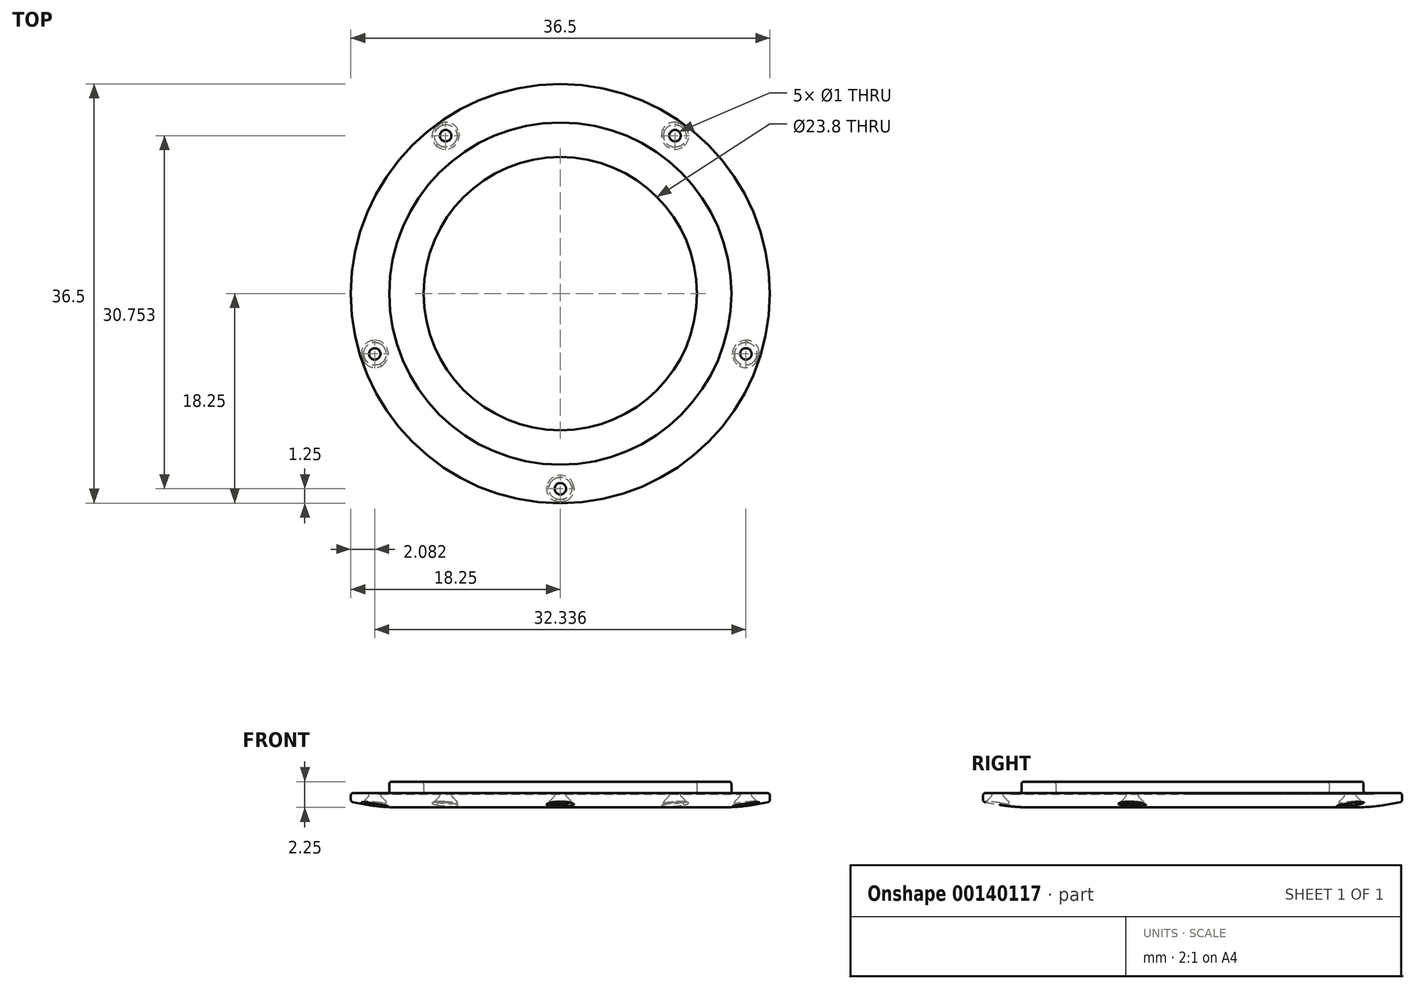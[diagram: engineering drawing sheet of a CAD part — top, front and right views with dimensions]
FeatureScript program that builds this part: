
annotation { "Feature Type Name" : "Feature", "Feature Type Description" : "" }
export const myFeature = defineFeature(function(context is Context, id is Id, definition is map)
    precondition{}
    {
        {
            var Q0;
            Q0=qCreatedBy(makeId("Front.planeOp"),FACE);
            var sketch = newSketch(context, id + "F0", { "sketchPlane" : qUnion([Q0])});
            skLineSegment(sketch, "E0", {"start": v(0, 0) * mm, "end": v(0, -1.25) * mm});
            skLineSegment(sketch, "E1", {"start": v(0, 0) * mm, "end": v(-11.7, 0) * mm});
            skLineSegment(sketch, "E2", {"start": v(-11.9, 0.2) * mm, "end": v(-11.9, 0.8) * mm});
            skLineSegment(sketch, "E3", {"start": v(-12.1, 1) * mm, "end": v(-14.7, 1) * mm});
            skLineSegment(sketch, "E4", {"start": v(-14.9, 0.8) * mm, "end": v(-14.9, 0.2) * mm});
            skLineSegment(sketch, "E5", {"start": v(-15.1, 0) * mm, "end": v(-15.47, 0) * mm});
            skLineSegment(sketch, "E6", {"start": v(-18.25, -0.2) * mm, "end": v(-18.25, -0.6) * mm});
            skLineSegment(sketch, "E7", {"start": v(-14, -1.25) * mm, "end": v(0, -1.25) * mm});
            skLineSegment(sketch, "E8", {"start": v(0, 0) * mm, "end": v(0, 1) * mm, "construction": true});
            skArc(sketch, "E9", {"start": v(-14, -1.25) * mm, "mid": v(-16.06, -1.13) * mm, "end": v(-18.1, -0.79) * mm});
            skPoint(sketch, "E10.visualSharp", {"position": v(-14.9, 0) * mm});
            skArc(sketch, "E10.filletArc", {"start": v(-15.1, 0) * mm, "mid": v(-14.96, 0.06) * mm, "end": v(-14.9, 0.2) * mm});
            skPoint(sketch, "E11.visualSharp", {"position": v(-14.9, 1) * mm});
            skArc(sketch, "E11.filletArc", {"start": v(-14.7, 1) * mm, "mid": v(-14.84, 0.94) * mm, "end": v(-14.9, 0.8) * mm});
            skPoint(sketch, "E12.visualSharp", {"position": v(-11.9, 0) * mm});
            skArc(sketch, "E12.filletArc", {"start": v(-11.9, 0.2) * mm, "mid": v(-11.84, 0.06) * mm, "end": v(-11.7, 0) * mm});
            skPoint(sketch, "E13.visualSharp", {"position": v(-18.25, 0) * mm});
            skArc(sketch, "E13.filletArc", {"start": v(-18.05, 0) * mm, "mid": v(-18.2, -0.06) * mm, "end": v(-18.25, -0.2) * mm});
            skPoint(sketch, "E14.visualSharp", {"position": v(-18.25, -0.75) * mm});
            skArc(sketch, "E14.filletArc", {"start": v(-18.25, -0.6) * mm, "mid": v(-18.2, -0.72) * mm, "end": v(-18.1, -0.79) * mm});
            skPoint(sketch, "E15.visualSharp", {"position": v(-11.9, 1) * mm});
            skArc(sketch, "E15.filletArc", {"start": v(-11.9, 0.8) * mm, "mid": v(-11.96, 0.94) * mm, "end": v(-12.1, 1) * mm});
            skPoint(sketch, "E16.visualSharp", {"position": v(0, -1.25) * mm});
            skArc(sketch, "E17", {"start": v(-15.9, -0.04) * mm, "mid": v(-15.75, -0.1) * mm, "end": v(-15.6, -0.04) * mm});
            skLineSegment(sketch, "E18.trimOffspring", {"start": v(-16.03, 0) * mm, "end": v(-18.05, 0) * mm});
            skPoint(sketch, "E19.visualSharp", {"position": v(-15.95, 0) * mm});
            skArc(sketch, "E19.filletArc", {"start": v(-15.9, -0.04) * mm, "mid": v(-15.97, -0.01) * mm, "end": v(-16.03, 0) * mm});
            skPoint(sketch, "E20.visualSharp", {"position": v(-15.55, 0) * mm});
            skArc(sketch, "E20.filletArc", {"start": v(-15.47, 0) * mm, "mid": v(-15.53, -0.01) * mm, "end": v(-15.6, -0.04) * mm});
            skSolve(sketch);
        }
        {
            var Q0;
            Q0=qSketchRegion(id+"F0",true);
            var Q1;
            Q1=sQuery(id+"F0.wireOp",EDGE,"E8");
            revolve(context, id + "F1", {"entities" : qUnion([Q0]), "axis" : qUnion([Q1]), "revolveType" : RevolveType.FULL});
        }
        {
            var Q0;
            Q0=qCreatedBy(makeId("Right.planeOp"),FACE);
            var sketch = newSketch(context, id + "F2", { "sketchPlane" : qUnion([Q0])});
            skLineSegment(sketch, "E21", {"start": v(-17, 0) * mm, "end": v(-17.5, 0) * mm});
            skLineSegment(sketch, "E22", {"start": v(-17, -1.25) * mm, "end": v(-18, -1.25) * mm});
            skLineSegment(sketch, "E23", {"start": v(-18, -1.25) * mm, "end": v(-18, -0.75) * mm});
            skLineSegment(sketch, "E24", {"start": v(-17, 0) * mm, "end": v(-17, 0.93) * mm, "construction": true});
            skLineSegment(sketch, "E25", {"start": v(-17, 0) * mm, "end": v(-17, -1.25) * mm});
            skLineSegment(sketch, "E26", {"start": v(-17.5, 0) * mm, "end": v(-17.5, -0.25) * mm});
            skLineSegment(sketch, "E27", {"start": v(-17.5, -0.25) * mm, "end": v(-18, -0.75) * mm});
            skSolve(sketch);
        }
        {
            var Q0;
            Q0=qSketchRegion(id+"F2",true);
            var Q1;
            Q1=makeQuery(id+"F2.imprint","IMPRINT",FACE,{"disambiguationData":[TD([[makeQuery(id+"F2.imprint","IMPRINT",EDGE,{"derivedFrom":sQuery(id+"F2.wireOp",EDGE,"E21")}),1.0]])]});
            var Q2;
            Q2=sQuery(id+"F2.wireOp",EDGE,"E24");
            revolve(context, id + "F3", {"entities" : qUnion([Q0, Q1]), "axis" : qUnion([Q2]), "revolveType" : RevolveType.FULL, "oppositeDirection" : true});
        }
        {
            var Q0;
            Q0=makeQuery(id+"F3.opRevolve","SWEPT_BODY",BODY,{"disambiguationData":[OSD([sQuery(id+"F2.wireOp",EDGE,"E21"),sQuery(id+"F2.wireOp",EDGE,"2oNXKCKB-Rh66-Nj45-adpD-4nFgSYGKnnpU"),sQuery(id+"F2.wireOp",EDGE,"E22"),sQuery(id+"F2.wireOp",EDGE,"E23"),sQuery(id+"F2.wireOp",EDGE,"tctMOU8y-Mgo1-Lk33-zD8C-WWPehcmeRYiv"),sQuery(id+"F2.wireOp",EDGE,"E25")])]});
            var Q1;
            Q1=makeQuery(id+"F1.opRevolve","SWEPT_EDGE",EDGE,{"disambiguationData":[OSD([sQuery(id+"F0.wireOp",EDGE,"E7"),sQuery(id+"F0.wireOp",EDGE,"E9")])]});
            circularPattern(context, id + "F4", {"operationType" : NewBodyOperationType.REMOVE, "entities" : qUnion([Q0]), "axis" : qUnion([Q1]), "angle" : 360 * degree, "instanceCount" : 5, "equalSpace" : true, "computeTransformsWithoutBuiltin" : true});
        }
        {
            var Q0;
            Q0=makeQuery(id+"F4.boolean.opBoolean","COPY",EDGE,{"derivedFrom":makeQuery(id+"F4.opPattern","COPY",EDGE,{"derivedFrom":makeQuery(id+"F3.opRevolve","SWEPT_EDGE",EDGE,{"disambiguationData":[OSD([sQuery(id+"F2.wireOp",EDGE,"E21"),sQuery(id+"F2.wireOp",EDGE,"tctMOU8y-Mgo1-Lk33-zD8C-WWPehcmeRYiv")])]}),"instanceName":"1"})});
            var Q1;
            Q1=makeQuery(id+"F4.boolean.opBoolean","COPY",EDGE,{"derivedFrom":makeQuery(id+"F3.opRevolve","SWEPT_EDGE",EDGE,{"disambiguationData":[OSD([sQuery(id+"F2.wireOp",EDGE,"E21"),sQuery(id+"F2.wireOp",EDGE,"tctMOU8y-Mgo1-Lk33-zD8C-WWPehcmeRYiv")])]})});
            var Q2;
            Q2=makeQuery(id+"F4.boolean.opBoolean","COPY",EDGE,{"derivedFrom":makeQuery(id+"F4.opPattern","COPY",EDGE,{"derivedFrom":makeQuery(id+"F3.opRevolve","SWEPT_EDGE",EDGE,{"disambiguationData":[OSD([sQuery(id+"F2.wireOp",EDGE,"E21"),sQuery(id+"F2.wireOp",EDGE,"tctMOU8y-Mgo1-Lk33-zD8C-WWPehcmeRYiv")])]}),"instanceName":"3"})});
            var Q3;
            Q3=makeQuery(id+"F4.boolean.opBoolean","COPY",EDGE,{"derivedFrom":makeQuery(id+"F4.opPattern","COPY",EDGE,{"derivedFrom":makeQuery(id+"F3.opRevolve","SWEPT_EDGE",EDGE,{"disambiguationData":[OSD([sQuery(id+"F2.wireOp",EDGE,"E21"),sQuery(id+"F2.wireOp",EDGE,"tctMOU8y-Mgo1-Lk33-zD8C-WWPehcmeRYiv")])]}),"instanceName":"2"})});
            var Q4;
            Q4=makeQuery(id+"F4.boolean.opBoolean","COPY",EDGE,{"derivedFrom":makeQuery(id+"F4.opPattern","COPY",EDGE,{"derivedFrom":makeQuery(id+"F3.opRevolve","SWEPT_EDGE",EDGE,{"disambiguationData":[OSD([sQuery(id+"F2.wireOp",EDGE,"E21"),sQuery(id+"F2.wireOp",EDGE,"tctMOU8y-Mgo1-Lk33-zD8C-WWPehcmeRYiv")])]}),"instanceName":"4"})});
            var Q5;
            Q5=makeQuery(id+"F4.boolean.opBoolean","COPY",EDGE,{"derivedFrom":makeQuery(id+"F3.opRevolve","SWEPT_EDGE",EDGE,{"disambiguationData":[OSD([sQuery(id+"F2.wireOp",EDGE,"E23"),sQuery(id+"F2.wireOp",EDGE,"E27")])]})});
            var Q6;
            Q6=makeQuery(id+"F4.boolean.opBoolean","COPY",EDGE,{"derivedFrom":makeQuery(id+"F4.opPattern","COPY",EDGE,{"derivedFrom":makeQuery(id+"F3.opRevolve","SWEPT_EDGE",EDGE,{"disambiguationData":[OSD([sQuery(id+"F2.wireOp",EDGE,"E23"),sQuery(id+"F2.wireOp",EDGE,"E27")])]}),"instanceName":"1"})});
            var Q7;
            Q7=makeQuery(id+"F4.boolean.opBoolean","COPY",EDGE,{"derivedFrom":makeQuery(id+"F4.opPattern","COPY",EDGE,{"derivedFrom":makeQuery(id+"F3.opRevolve","SWEPT_EDGE",EDGE,{"disambiguationData":[OSD([sQuery(id+"F2.wireOp",EDGE,"E23"),sQuery(id+"F2.wireOp",EDGE,"E27")])]}),"instanceName":"2"})});
            var Q8;
            Q8=makeQuery(id+"F4.boolean.opBoolean","COPY",EDGE,{"derivedFrom":makeQuery(id+"F4.opPattern","COPY",EDGE,{"derivedFrom":makeQuery(id+"F3.opRevolve","SWEPT_EDGE",EDGE,{"disambiguationData":[OSD([sQuery(id+"F2.wireOp",EDGE,"E23"),sQuery(id+"F2.wireOp",EDGE,"E27")])]}),"instanceName":"3"})});
            var Q9;
            Q9=makeQuery(id+"F4.boolean.opBoolean","COPY",EDGE,{"derivedFrom":makeQuery(id+"F4.opPattern","COPY",EDGE,{"derivedFrom":makeQuery(id+"F3.opRevolve","SWEPT_EDGE",EDGE,{"disambiguationData":[OSD([sQuery(id+"F2.wireOp",EDGE,"E23"),sQuery(id+"F2.wireOp",EDGE,"E27")])]}),"instanceName":"4"})});
            fillet(context, id + "F5", {"entities" : qUnion([Q0, Q1, Q2, Q3, Q4, Q5, Q6, Q7, Q8, Q9]), "radius" : 0.2 * mm, "tangentPropagation" : true, "allowEdgeOverflow" : false});
        }
        {
            var Q0;
            Q0=makeQuery(id+"F4.boolean.opBoolean","INTERSECT",EDGE,{"derivedFrom":[makeQuery(id+"F1.opRevolve","SWEPT_FACE",FACE,{"disambiguationData":[OSD([sQuery(id+"F0.wireOp",EDGE,"E9")])]}),makeQuery(id+"F3.opRevolve","SWEPT_FACE",FACE,{"disambiguationData":[OSD([sQuery(id+"F2.wireOp",EDGE,"E23")])]})]});
            var Q1;
            Q1=makeQuery(id+"F4.boolean.opBoolean","INTERSECT",EDGE,{"derivedFrom":[makeQuery(id+"F1.opRevolve","SWEPT_FACE",FACE,{"disambiguationData":[OSD([sQuery(id+"F0.wireOp",EDGE,"E9")])]}),makeQuery(id+"F4.opPattern","COPY",FACE,{"derivedFrom":makeQuery(id+"F3.opRevolve","SWEPT_FACE",FACE,{"disambiguationData":[OSD([sQuery(id+"F2.wireOp",EDGE,"E23")])]}),"instanceName":"1"})]});
            var Q2;
            Q2=makeQuery(id+"F4.boolean.opBoolean","INTERSECT",EDGE,{"derivedFrom":[makeQuery(id+"F1.opRevolve","SWEPT_FACE",FACE,{"disambiguationData":[OSD([sQuery(id+"F0.wireOp",EDGE,"E9")])]}),makeQuery(id+"F4.opPattern","COPY",FACE,{"derivedFrom":makeQuery(id+"F3.opRevolve","SWEPT_FACE",FACE,{"disambiguationData":[OSD([sQuery(id+"F2.wireOp",EDGE,"E23")])]}),"instanceName":"4"})]});
            var Q3;
            Q3=makeQuery(id+"F4.boolean.opBoolean","INTERSECT",EDGE,{"derivedFrom":[makeQuery(id+"F1.opRevolve","SWEPT_FACE",FACE,{"disambiguationData":[OSD([sQuery(id+"F0.wireOp",EDGE,"E9")])]}),makeQuery(id+"F4.opPattern","COPY",FACE,{"derivedFrom":makeQuery(id+"F3.opRevolve","SWEPT_FACE",FACE,{"disambiguationData":[OSD([sQuery(id+"F2.wireOp",EDGE,"E23")])]}),"instanceName":"2"})]});
            var Q4;
            Q4=makeQuery(id+"F4.boolean.opBoolean","INTERSECT",EDGE,{"derivedFrom":[makeQuery(id+"F1.opRevolve","SWEPT_FACE",FACE,{"disambiguationData":[OSD([sQuery(id+"F0.wireOp",EDGE,"E9")])]}),makeQuery(id+"F4.opPattern","COPY",FACE,{"derivedFrom":makeQuery(id+"F3.opRevolve","SWEPT_FACE",FACE,{"disambiguationData":[OSD([sQuery(id+"F2.wireOp",EDGE,"E23")])]}),"instanceName":"3"})]});
            var Q5;
            Q5=makeQuery(id+"F4.boolean.opBoolean","COPY",EDGE,{"derivedFrom":makeQuery(id+"F3.opRevolve","SWEPT_EDGE",EDGE,{"disambiguationData":[OSD([sQuery(id+"F2.wireOp",EDGE,"E26"),sQuery(id+"F2.wireOp",EDGE,"E27")])]})});
            var Q6;
            Q6=makeQuery(id+"F4.boolean.opBoolean","COPY",EDGE,{"derivedFrom":makeQuery(id+"F4.opPattern","COPY",EDGE,{"derivedFrom":makeQuery(id+"F3.opRevolve","SWEPT_EDGE",EDGE,{"disambiguationData":[OSD([sQuery(id+"F2.wireOp",EDGE,"E26"),sQuery(id+"F2.wireOp",EDGE,"E27")])]}),"instanceName":"1"})});
            var Q7;
            Q7=makeQuery(id+"F4.boolean.opBoolean","COPY",EDGE,{"derivedFrom":makeQuery(id+"F4.opPattern","COPY",EDGE,{"derivedFrom":makeQuery(id+"F3.opRevolve","SWEPT_EDGE",EDGE,{"disambiguationData":[OSD([sQuery(id+"F2.wireOp",EDGE,"E26"),sQuery(id+"F2.wireOp",EDGE,"E27")])]}),"instanceName":"2"})});
            var Q8;
            Q8=makeQuery(id+"F4.boolean.opBoolean","COPY",EDGE,{"derivedFrom":makeQuery(id+"F4.opPattern","COPY",EDGE,{"derivedFrom":makeQuery(id+"F3.opRevolve","SWEPT_EDGE",EDGE,{"disambiguationData":[OSD([sQuery(id+"F2.wireOp",EDGE,"E26"),sQuery(id+"F2.wireOp",EDGE,"E27")])]}),"instanceName":"3"})});
            var Q9;
            Q9=makeQuery(id+"F4.boolean.opBoolean","COPY",EDGE,{"derivedFrom":makeQuery(id+"F4.opPattern","COPY",EDGE,{"derivedFrom":makeQuery(id+"F3.opRevolve","SWEPT_EDGE",EDGE,{"disambiguationData":[OSD([sQuery(id+"F2.wireOp",EDGE,"E26"),sQuery(id+"F2.wireOp",EDGE,"E27")])]}),"instanceName":"4"})});
            fillet(context, id + "F6", {"entities" : qUnion([Q0, Q1, Q2, Q3, Q4, Q5, Q6, Q7, Q8, Q9]), "radius" : 0.2 * mm, "tangentPropagation" : true, "allowEdgeOverflow" : false});
        }
    });
